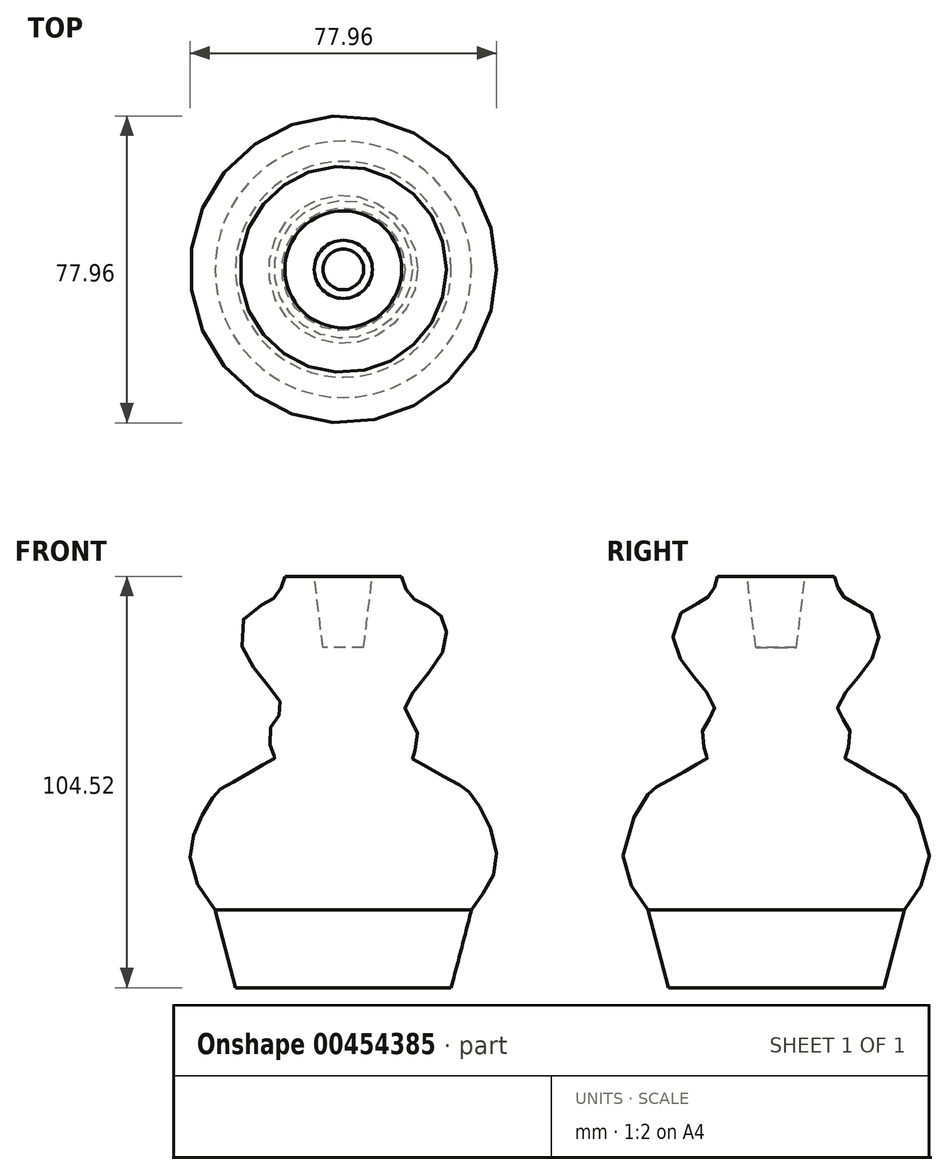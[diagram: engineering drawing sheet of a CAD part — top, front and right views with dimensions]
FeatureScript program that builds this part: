
annotation { "Feature Type Name" : "Feature", "Feature Type Description" : "" }
export const myFeature = defineFeature(function(context is Context, id is Id, definition is map)
    precondition{}
    {
        {
            var Q0;
            Q0=qCreatedBy(makeId("Front.planeOp"),FACE);
            var sketch = newSketch(context, id + "F0", { "sketchPlane" : qUnion([Q0])});
            skLineSegment(sketch, "E0", {"start": v(0, 0) * mm, "end": v(27.41, 0) * mm});
            skLineSegment(sketch, "E1", {"start": v(27.41, 0) * mm, "end": v(32.56, 19.7) * mm});
            skFitSpline(sketch, "E2", {"points": [v(32.56, 19.7) * mm, v(38.97, 32.5) * mm, v(32.56, 49.12) * mm, v(27.99, 52.26) * mm, v(17.65, 58.11) * mm, v(17.52, 58.2) * mm, v(18.76, 65.26) * mm, v(15.63, 71.02) * mm, v(24.84, 84.53) * mm, v(24.27, 95.1) * mm, v(17.42, 99.1) * mm, v(14.85, 104.52) * mm], "startDerivative": vector(59.42, 94.8) * mm, "endDerivative": vector(-19.55, 77.7) * mm});
            skLineSegment(sketch, "E3", {"start": v(14.85, 104.52) * mm, "end": v(7.39, 104.52) * mm});
            skLineSegment(sketch, "E4", {"start": v(7.39, 104.52) * mm, "end": v(5.18, 86.49) * mm});
            skLineSegment(sketch, "E5", {"start": v(5.18, 86.49) * mm, "end": v(0, 86.49) * mm});
            skPoint(sketch, "E6.orphan", {"position": v(0, 51.69) * mm});
            skLineSegment(sketch, "E7", {"start": v(0, 86.49) * mm, "end": v(0, 0) * mm});
            skSolve(sketch);
        }
        {
            var Q0;
            Q0=makeQuery(id+"F0.imprint","IMPRINT",FACE,{"disambiguationData":[TD([[makeQuery(id+"F0.imprint","IMPRINT",EDGE,{"derivedFrom":sQuery(id+"F0.wireOp",EDGE,"E0")}),1.0]])]});
            var Q1;
            Q1=sQuery(id+"F0.wireOp",EDGE,"E7");
            revolve(context, id + "F1", {"entities" : qUnion([Q0]), "axis" : qUnion([Q1]), "revolveType" : RevolveType.FULL});
        }
    });
